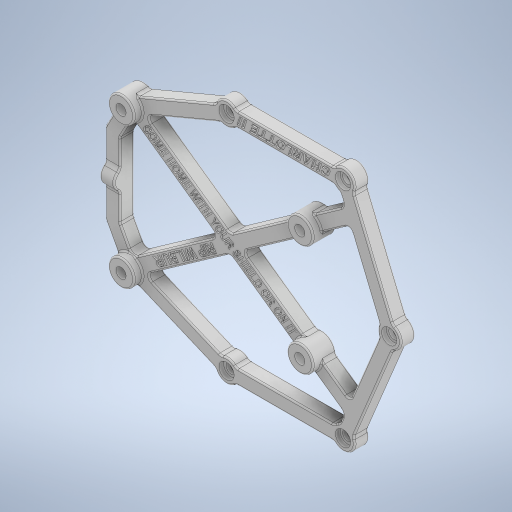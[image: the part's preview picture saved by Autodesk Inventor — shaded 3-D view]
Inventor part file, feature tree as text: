
AUTODESK INVENTOR PART (.ipt)
format: ipt  version: 2024.2 (Build 282272000, 272)  size: 1,875,968 bytes
history: native  units: mm
features: sketch x12, reference x8, extrude x7, fillet x4, hole x3, emboss x3, other x3, projected_geometry x1
ambient origin geometry x8: Origin, YZ Plane, XZ Plane, XY Plane, X Axis, Y Axis, Z Axis, Center Point
bodies: Solid1 (feature_tree)
feature tree (41):
  extrude  "Extrusion1"  Depth=9.0mm
  extrude  "Extrusion2"  Depth=5.25mm
  extrude  "Extrusion3"  Depth=49.0mm
  extrude  "Extrusion4"  Depth=5.0mm
  hole  "Hole1"  [1 undecoded]
  hole  "Hole3"  [1 undecoded]
  fillet  "Fillet1"  Radius=2.5mm
  fillet  "Fillet2"  Radius=2.5mm
  sketch  "Sketch7"  dims[d10=5.0mm d11=5.0mm d12=2.5mm d13=2.5mm]
  extrude  "Extrusion5"  Depth=2.5mm
  fillet  "Fillet3"  Radius=2.5mm
  hole  "Hole2"  [1 undecoded]
  fillet  "Fillet4"  Radius=5.0mm
  emboss  "Emboss1"
  emboss  "Emboss2"
  emboss  "Emboss3"
  extrude  "Extrusion6"  Depth=5.0mm TaperAngle=0.0deg
  extrude  "Extrusion7"  Depth=2.0mm
  sketch  "Sketch1"  dims[d0=8.0mm d1=9.0mm]
  reference  "Reference1"
  reference  "Reference2"
  reference  "Reference3"
  reference  "Reference4"
  reference  "Reference5"
  reference  "Reference6"
  reference  "Reference7"
  reference  "Reference8"
  sketch  "Sketch3"  dims[d2=5.25mm d3=5.25mm]
  projected_geometry  "Projected Loop1"
  sketch  "Sketch4"  dims[d4=62.0mm d5=49.0mm]
  sketch  "Sketch5"  dims[d6=28.0mm d7=5.0mm]
  sketch  "Sketch6"  dims[d8=2.5mm d9=2.5mm]
  sketch  "Sketch9"  dims[d14=5.0mm d15=2.5mm d16=2.5mm]
  sketch  "Sketch10"  dims[d17=5.0mm d18=5.6mm d19=5.0mm d20=0.0mm]
  sketch  "Sketch11"  dims[d21=1.9mm d22=0.0mm d23=5.0mm d24=0.0mm]
  sketch  "Sketch12"  dims[d25=3.0mm d26=0.0mm]
  sketch  "Sketch13"  dims[d27=3.5mm d28=6.0mm d29=4.0mm d30=2.0mm d31=90.0deg d32=2.0mm d33=0.0mm d34=2.0mm]
  sketch  "Sketch14"  dims[d35=1.5mm d36=7.0mm d37=3.0mm d38=0.0mm d39=2.0mm d40=2.8mm d41=6.0mm d42=4.0mm d43=2.0mm d44=90.0deg d45=4.0mm d46=0.0mm d47=0.5mm d48=0.5mm d49=0.0mm d50=5.25mm d51=6.0mm d52=4.0mm d53=2.0mm d54=90.0deg d55=1.6mm d56=0.0mm d57=0.5mm d58=0.0mm d59=0.5mm d60=0.0mm d61=2.5mm d62=2.5mm d63=5.0mm d64=2.5mm d65=2.5mm d66=5.0mm d67=0.2mm d68=0.0mm d69=0.2mm d70=0.0mm]
  other  "<userpath>\Desktop\scioly-robot-tour\Hardware\ipt\v4\v4assembly.iam"
  other  "v4assembly.iam"
  other  "v4chassisv2:1"
note: 3 required parameter values undecoded (feature->parameter linkage not recoverable at this tier; creation-order binding heuristic only, values carry confidence <= 0.55)
